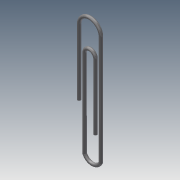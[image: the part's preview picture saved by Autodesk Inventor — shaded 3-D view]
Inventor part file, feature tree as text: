
AUTODESK INVENTOR PART (.ipt)
format: ipt  version: 2015 (Build 190159000, 159)  size: 121,856 bytes
history: native  units: in
note: dims shown in document units (in); Inventor stores cm internally (conversion verified against a paired STEP export)
features: sketch x2, plane x1, sweep x1
ambient origin geometry x8: Origin, YZ Plane, XZ Plane, XY Plane, X Axis, Y Axis, Z Axis, Center Point
bodies: Solid1 (feature_tree)
feature tree (4):
  sketch  "Sketch1"  dims[d7=0.15in d8=0.0in d9=0.0in]
  plane  "Work Plane1"
  sweep  "Sweep1"
  sketch  "Sketch2"
